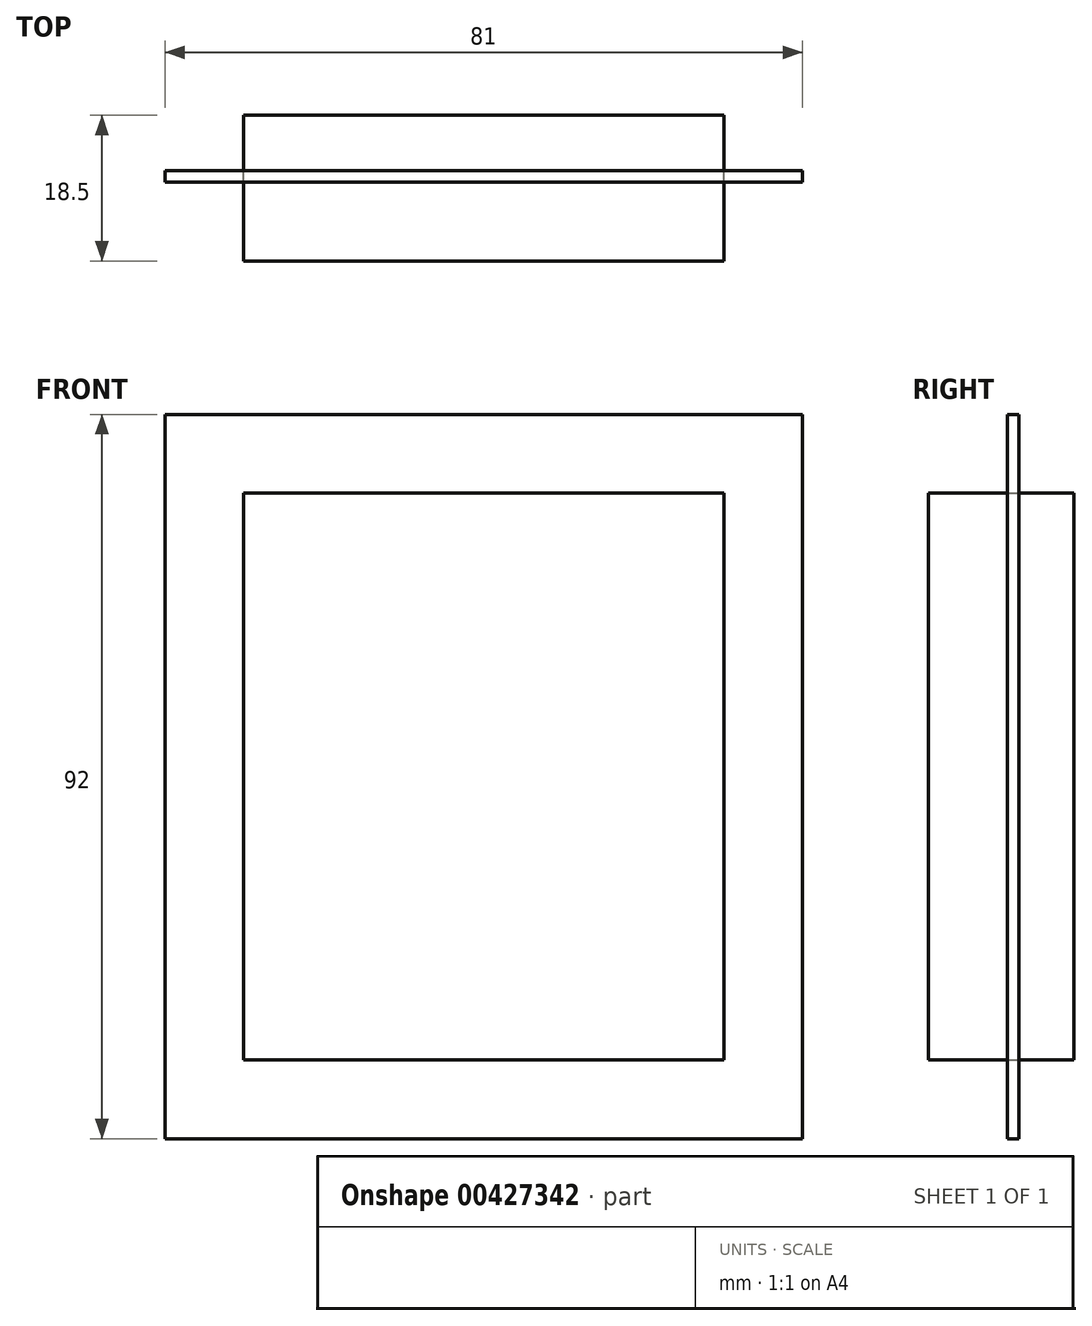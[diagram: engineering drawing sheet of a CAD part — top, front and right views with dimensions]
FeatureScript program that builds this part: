
annotation { "Feature Type Name" : "Feature", "Feature Type Description" : "" }
export const myFeature = defineFeature(function(context is Context, id is Id, definition is map)
    precondition{}
    {
        {
            var Q0;
            Q0=qCreatedBy(makeId("Front.planeOp"),FACE);
            var sketch = newSketch(context, id + "F0", { "sketchPlane" : qUnion([Q0])});
            skLineSegment(sketch, "E0.bottom", {"start": v(40.5, -36) * mm, "end": v(-40.5, -36) * mm});
            skLineSegment(sketch, "E0.top", {"start": v(40.5, 56) * mm, "end": v(-40.5, 56) * mm});
            skLineSegment(sketch, "E0.left", {"start": v(40.5, -36) * mm, "end": v(40.5, 56) * mm});
            skLineSegment(sketch, "E0.right", {"start": v(-40.5, -36) * mm, "end": v(-40.5, 56) * mm});
            skPoint(sketch, "E0.middle", {"position": v(0, 10) * mm});
            skSolve(sketch);
        }
        {
            var Q0;
            Q0=makeQuery(id+"F0.imprint","IMPRINT",FACE,{"disambiguationData":[TD([[makeQuery(id+"F0.imprint","IMPRINT",EDGE,{"derivedFrom":sQuery(id+"F0.wireOp",EDGE,"E0.bottom")}),-1.0]])]});
            extrude(context, id + "F1", {"entities" : qUnion([Q0]), "depth" : 1.5 * mm});
        }
        {
            var Q0;
            Q0=makeQuery(id+"F1.opExtrude","CAP_FACE",FACE,{"disambiguationData":[OSD([sQuery(id+"F0.wireOp",EDGE,"E0.bottom"),sQuery(id+"F0.wireOp",EDGE,"E0.top"),sQuery(id+"F0.wireOp",EDGE,"E0.left"),sQuery(id+"F0.wireOp",EDGE,"E0.right")])],"isStart":false});
            var sketch = newSketch(context, id + "F2", { "sketchPlane" : qUnion([Q0])});
            skLineSegment(sketch, "E1.0", {"start": v(-30.5, -26) * mm, "end": v(-30.5, 46) * mm});
            skLineSegment(sketch, "E1.1", {"start": v(30.5, -26) * mm, "end": v(-30.5, -26) * mm});
            skLineSegment(sketch, "E1.2", {"start": v(30.5, -26) * mm, "end": v(30.5, 46) * mm});
            skLineSegment(sketch, "E1.3", {"start": v(30.5, 46) * mm, "end": v(-30.5, 46) * mm});
            skSolve(sketch);
        }
        {
            var Q0;
            Q0 = qSketchRegion(id + "F2", true);
            extrude(context, id + "F3", {"entities" : qUnion([Q0]), "depth" : 10 * mm, "hasSecondDirection" : true, "secondDirectionOppositeDirection" : true, "secondDirectionDepth" : 8.5 * mm});
        }
    });
